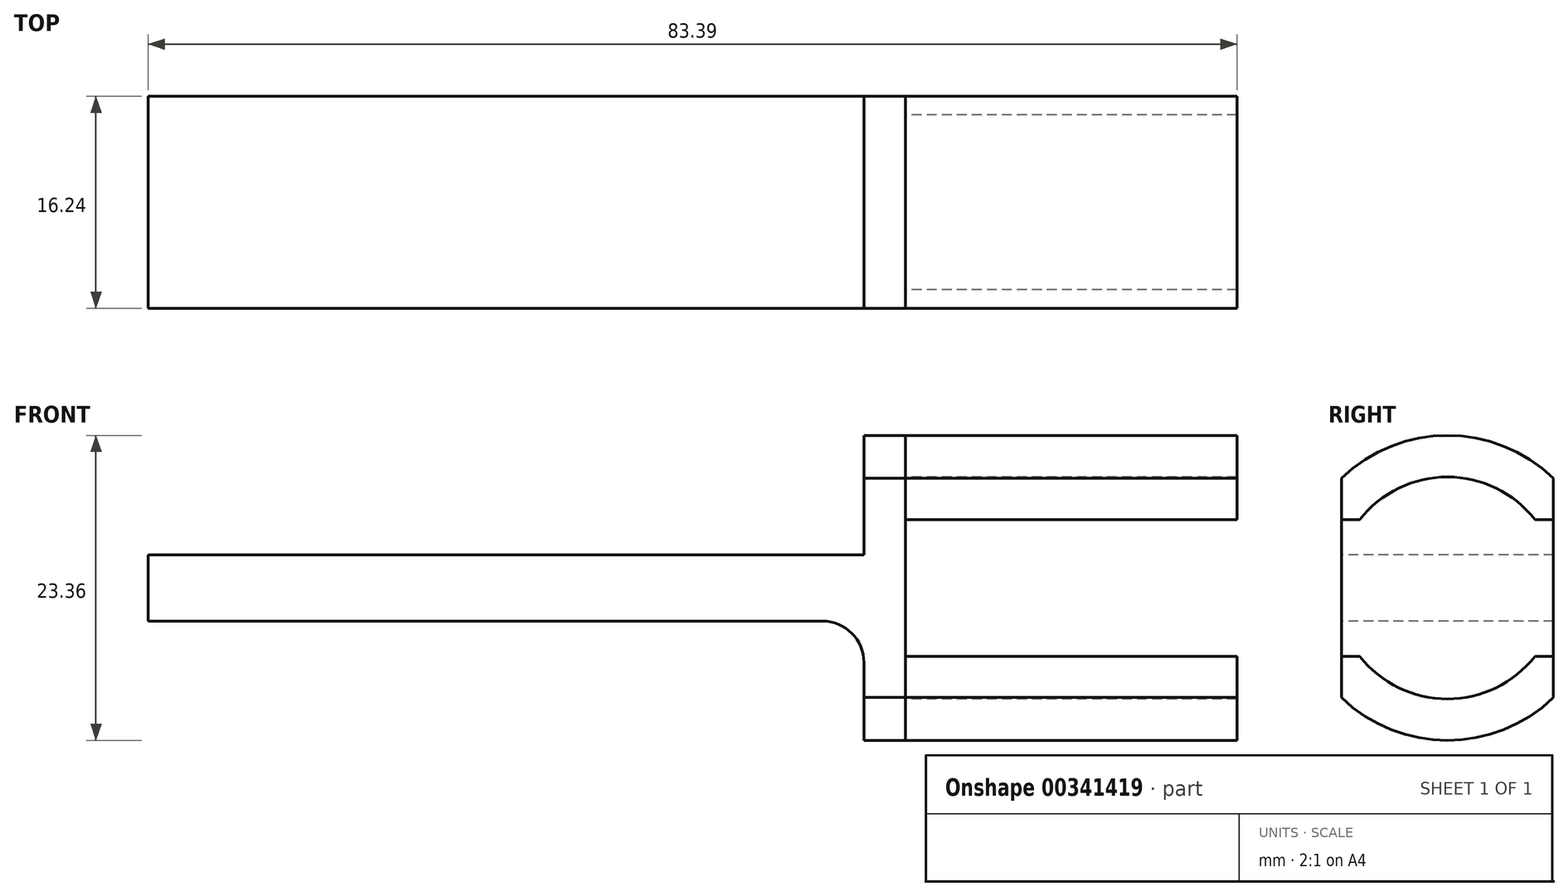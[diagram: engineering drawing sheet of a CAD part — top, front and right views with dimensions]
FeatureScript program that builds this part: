
annotation { "Feature Type Name" : "Feature", "Feature Type Description" : "" }
export const myFeature = defineFeature(function(context is Context, id is Id, definition is map)
    precondition{}
    {
        {
            var Q0;
            Q0=qCreatedBy(makeId("Right.planeOp"),FACE);
            var sketch = newSketch(context, id + "F0", { "sketchPlane" : qUnion([Q0])});
            skArc(sketch, "E0", {"start": v(-8.12, -8.4) * mm, "mid": v(0, -11.68) * mm, "end": v(8.12, -8.4) * mm});
            skArc(sketch, "E1", {"start": v(-6.7, -5.24) * mm, "mid": v(0, -8.5) * mm, "end": v(6.7, -5.24) * mm});
            skLineSegment(sketch, "E2", {"start": v(8.12, 8.4) * mm, "end": v(8.12, -8.4) * mm});
            skLineSegment(sketch, "E3.MirrorCS", {"start": v(-8.12, 8.4) * mm, "end": v(-8.12, -8.4) * mm});
            skArc(sketch, "E4.trimOffspring", {"start": v(8.12, 8.4) * mm, "mid": v(0, 11.68) * mm, "end": v(-8.12, 8.4) * mm});
            skArc(sketch, "E5.trimOffspring", {"start": v(6.7, 5.24) * mm, "mid": v(0, 8.5) * mm, "end": v(-6.7, 5.24) * mm});
            skLineSegment(sketch, "E6", {"start": v(-8.12, 5.24) * mm, "end": v(-6.7, 5.24) * mm});
            skLineSegment(sketch, "E7.trimOffspring", {"start": v(6.7, 5.24) * mm, "end": v(8.12, 5.24) * mm});
            skLineSegment(sketch, "E8.MirrorCS", {"start": v(-8.12, -5.24) * mm, "end": v(-6.7, -5.24) * mm});
            skLineSegment(sketch, "E9.MirrorCS", {"start": v(6.7, -5.24) * mm, "end": v(8.12, -5.24) * mm});
            skSolve(sketch);
        }
        {
            var Q0;
            {var subQ0=sQuery(id+"F0.wireOp",EDGE,"E4.trimOffspring");Q0=makeQuery(id+"F0.imprint","IMPRINT",FACE,{"disambiguationData":[TD([[makeQuery(id+"F0.imprint","IMPRINT",EDGE,{"derivedFrom":subQ0}),1.0]])]});}
            var Q1;
            {var subQ0=sQuery(id+"F0.wireOp",EDGE,"E0");Q1=makeQuery(id+"F0.imprint","IMPRINT",FACE,{"disambiguationData":[TD([[makeQuery(id+"F0.imprint","IMPRINT",EDGE,{"derivedFrom":subQ0}),1.0]])]});}
            extrude(context, id + "F1", {"entities" : qUnion([Q0, Q1]), "depth" : 25.4 * mm});
        }
        {
            var Q0;
            Q0=makeQuery(id+"F0.imprint","IMPRINT",FACE,{"disambiguationData":[TD([[makeQuery(id+"F0.imprint","IMPRINT",EDGE,{"derivedFrom":sQuery(id+"F0.wireOp",EDGE,"E1")}),1.0]])]});
            var Q1;
            {var subQ0=sQuery(id+"F0.wireOp",EDGE,"E4.trimOffspring");Q1=makeQuery(id+"F0.imprint","IMPRINT",FACE,{"disambiguationData":[TD([[makeQuery(id+"F0.imprint","IMPRINT",EDGE,{"derivedFrom":subQ0}),1.0]])]});}
            var Q2;
            {var subQ1=sQuery(id+"F0.wireOp",EDGE,"E0");Q2=makeQuery(id+"F0.imprint","IMPRINT",FACE,{"disambiguationData":[TD([[makeQuery(id+"F0.imprint","IMPRINT",EDGE,{"derivedFrom":subQ1}),1.0]])]});}
            extrude(context, id + "F2", {"entities" : qUnion([Q0, Q1, Q2]), "oppositeDirection" : true, "depth" : 3.17 * mm});
        }
        {
            var Q0;
            Q0=makeQuery(id+"F2.opExtrude","CAP_FACE",FACE,{"disambiguationData":[OSD([sQuery(id+"F0.wireOp",EDGE,"E0"),sQuery(id+"F0.wireOp",EDGE,"E2"),sQuery(id+"F0.wireOp",EDGE,"E3.MirrorCS"),sQuery(id+"F0.wireOp",EDGE,"E4.trimOffspring")])],"isStart":false});
            var sketch = newSketch(context, id + "F3", { "sketchPlane" : qUnion([Q0])});
            skLineSegment(sketch, "E10.bottom", {"start": v(-8.12, -2.54) * mm, "end": v(8.12, -2.54) * mm});
            skLineSegment(sketch, "E10.top", {"start": v(-8.12, 2.54) * mm, "end": v(8.12, 2.54) * mm});
            skLineSegment(sketch, "E10.left", {"start": v(-8.12, -2.54) * mm, "end": v(-8.12, 2.54) * mm});
            skLineSegment(sketch, "E10.right", {"start": v(8.12, -2.54) * mm, "end": v(8.12, 2.54) * mm});
            skSolve(sketch);
        }
        {
            var Q0;
            Q0=makeQuery(id+"F3.imprint","IMPRINT",FACE,{"disambiguationData":[TD([[makeQuery(id+"F3.imprint","IMPRINT",EDGE,{"derivedFrom":sQuery(id+"F3.wireOp",EDGE,"E10.bottom")}),1.0]])]});
            extrude(context, id + "F4", {"entities" : qUnion([Q0]), "operationType" : NewBodyOperationType.ADD, "depth" : 54.81 * mm});
        }
        {
            var Q0;
            Q0=makeQuery(id+"F4.opExtrude","CAP_EDGE",EDGE,{"disambiguationData":[OSD([sQuery(id+"F3.wireOp",EDGE,"E10.top")])],"isStart":true});
            var Q1;
            Q1=makeQuery(id+"F4.opExtrude","CAP_EDGE",EDGE,{"disambiguationData":[OSD([sQuery(id+"F3.wireOp",EDGE,"E10.bottom")])],"isStart":true});
            fillet(context, id + "F5", {"entities" : qUnion([Q0, Q1]), "radius" : 3.17 * mm, "tangentPropagation" : true, "allowEdgeOverflow" : false});
        }
    });
